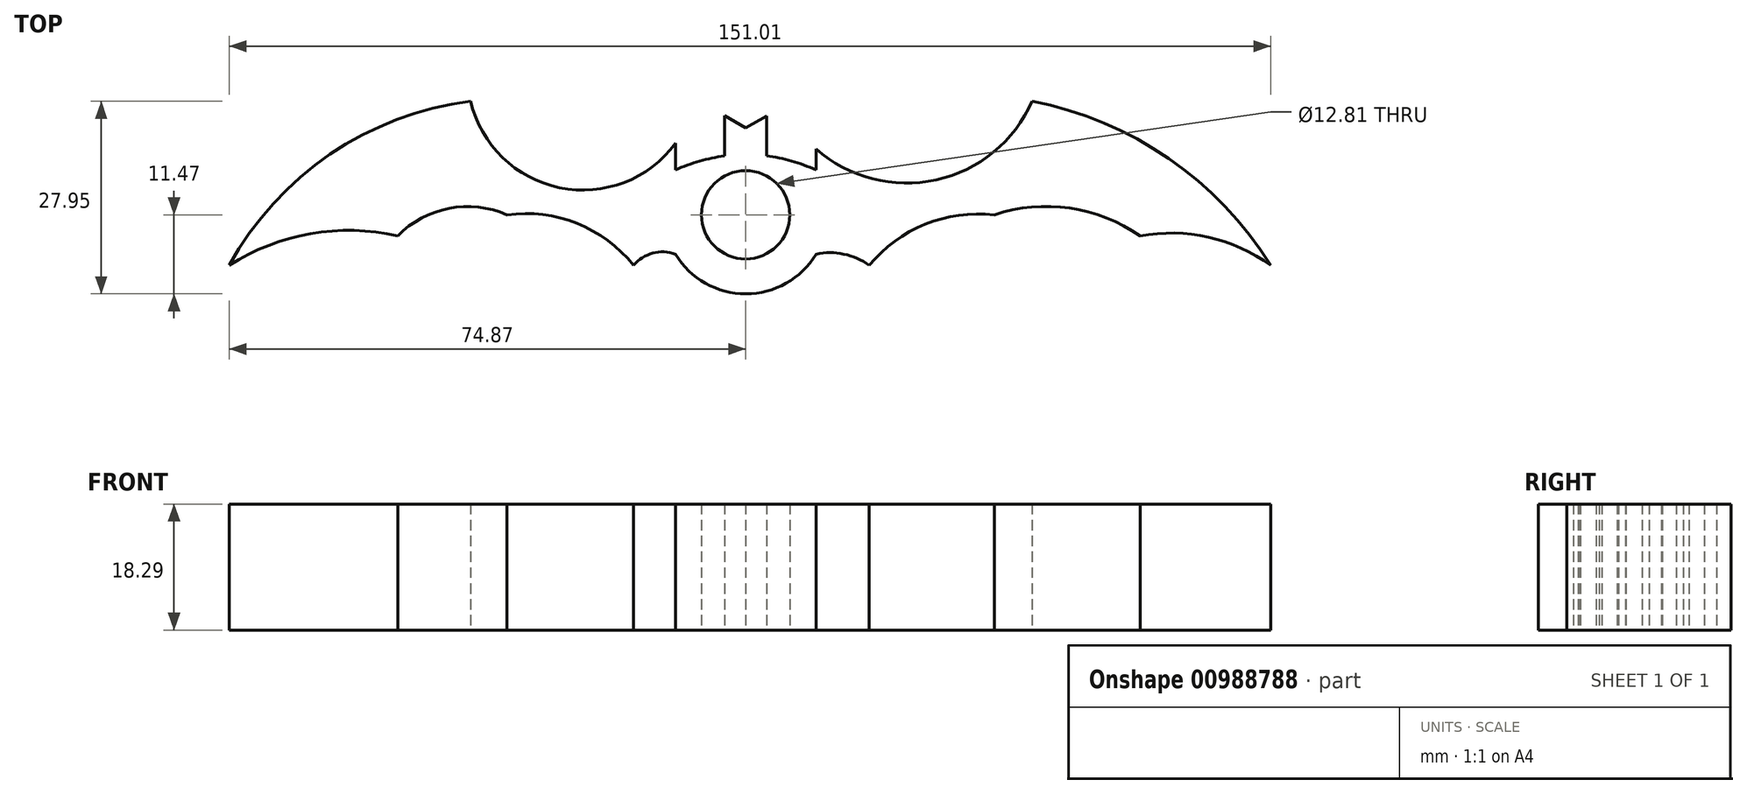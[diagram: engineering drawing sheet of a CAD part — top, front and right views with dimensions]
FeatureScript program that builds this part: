
annotation { "Feature Type Name" : "Feature", "Feature Type Description" : "" }
export const myFeature = defineFeature(function(context is Context, id is Id, definition is map)
    precondition{}
    {
        {
            var Q0;
            Q0=qCreatedBy(makeId("Top.planeOp"),FACE);
            var sketch = newSketch(context, id + "F0", { "sketchPlane" : qUnion([Q0])});
            skArc(sketch, "E0", {"start": v(-39.86, 16.48) * mm, "mid": v(-60.24, 8.8) * mm, "end": v(-74.87, -7.33) * mm});
            skArc(sketch, "E1", {"start": v(-39.86, 16.48) * mm, "mid": v(-26.96, 3.94) * mm, "end": v(-10.15, 10.37) * mm});
            skLineSegment(sketch, "E2", {"start": v(-10.15, 10.37) * mm, "end": v(-10.15, 6.5) * mm});
            skArc(sketch, "E3", {"start": v(10.2, 6.5) * mm, "mid": v(0.02, 8.75) * mm, "end": v(-10.15, 6.5) * mm});
            skLineSegment(sketch, "E4", {"start": v(10.2, 6.5) * mm, "end": v(10.2, 9.56) * mm});
            skArc(sketch, "E5", {"start": v(10.2, 9.56) * mm, "mid": v(27.63, 5.07) * mm, "end": v(41.54, 16.48) * mm});
            skArc(sketch, "E6", {"start": v(76.14, -7.33) * mm, "mid": v(61.33, 8.2) * mm, "end": v(41.54, 16.48) * mm});
            skArc(sketch, "E7", {"start": v(76.14, -7.33) * mm, "mid": v(67.11, -3.25) * mm, "end": v(57.21, -3.06) * mm});
            skArc(sketch, "E8", {"start": v(57.21, -3.06) * mm, "mid": v(47, 0.98) * mm, "end": v(36.05, 0) * mm});
            skArc(sketch, "E9", {"start": v(36.05, 0) * mm, "mid": v(26.06, -1.36) * mm, "end": v(17.93, -7.33) * mm});
            skArc(sketch, "E10", {"start": v(17.93, -7.33) * mm, "mid": v(14.24, -5.7) * mm, "end": v(10.2, -5.7) * mm});
            skArc(sketch, "E11", {"start": v(-10.15, -5.7) * mm, "mid": v(0.02, -11.47) * mm, "end": v(10.2, -5.7) * mm});
            skArc(sketch, "E12", {"start": v(-10.15, -5.7) * mm, "mid": v(-13.46, -5.55) * mm, "end": v(-16.26, -7.33) * mm});
            skArc(sketch, "E13", {"start": v(-16.26, -7.33) * mm, "mid": v(-24.44, -1.24) * mm, "end": v(-34.57, 0) * mm});
            skArc(sketch, "E14", {"start": v(-34.57, 0) * mm, "mid": v(-42.99, 0.94) * mm, "end": v(-50.45, -3.06) * mm});
            skArc(sketch, "E15", {"start": v(-50.45, -3.06) * mm, "mid": v(-63.09, -2.74) * mm, "end": v(-74.87, -7.33) * mm});
            skCircle(sketch, "E16", {"center": v(0, 0) * mm, "radius": 6.4 * mm});
            skLineSegment(sketch, "E17", {"start": v(-3.06, 8.55) * mm, "end": v(-3.06, 14.39) * mm});
            skLineSegment(sketch, "E18", {"start": v(-3.06, 14.39) * mm, "end": v(0, 12.6) * mm});
            skLineSegment(sketch, "E19", {"start": v(0, 12.6) * mm, "end": v(3.02, 14.37) * mm});
            skLineSegment(sketch, "E20", {"start": v(3.02, 14.37) * mm, "end": v(3.02, 8.56) * mm});
            skSolve(sketch);
        }
        {
            var Q0;
            Q0 = qSketchRegion(id + "F0", true);
            extrude(context, id + "F1", {"entities" : qUnion([Q0]), "depth" : 18.29 * mm, "offsetDistance" : 25.4 * mm});
        }
        {
            var Q0;
            Q0 = qSketchRegion(id + "F0", true);
            extrude(context, id + "F2", {"entities" : qUnion([Q0]), "operationType" : NewBodyOperationType.ADD, "depth" : 6.35 * mm, "offsetDistance" : 25.4 * mm});
        }
    });
